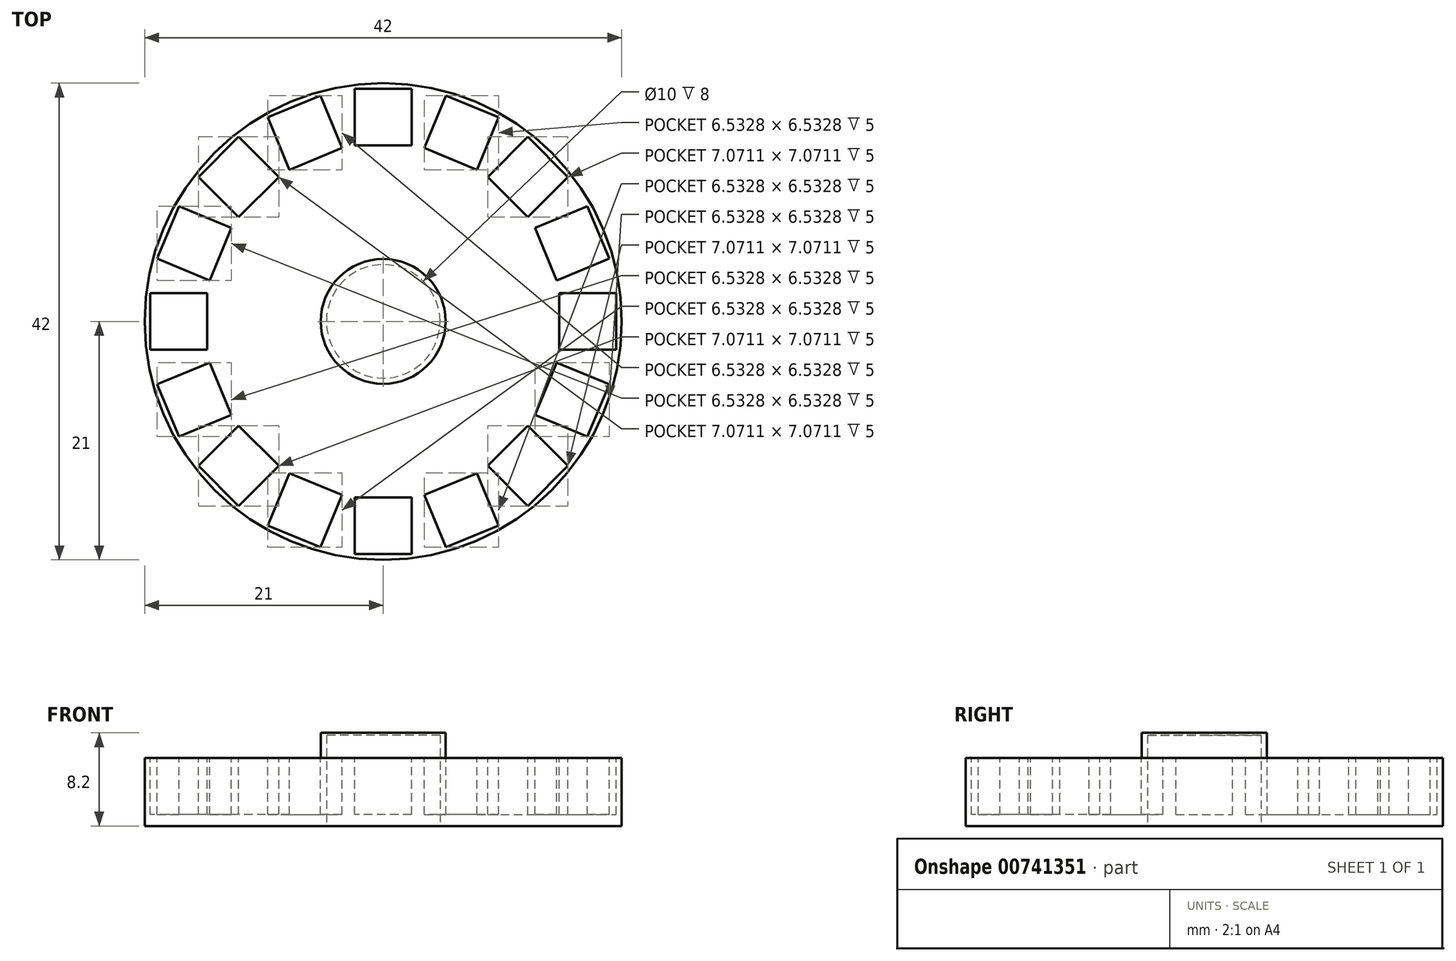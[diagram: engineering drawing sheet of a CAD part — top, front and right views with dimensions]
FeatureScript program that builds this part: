
annotation { "Feature Type Name" : "Feature", "Feature Type Description" : "" }
export const myFeature = defineFeature(function(context is Context, id is Id, definition is map)
    precondition{}
    {
        {
            var Q0;
            Q0=qCreatedBy(makeId("Front.planeOp"),FACE);
            var sketch = newSketch(context, id + "F0", { "sketchPlane" : qUnion([Q0])});
            skLineSegment(sketch, "E0", {"start": v(0, 0) * mm, "end": v(21, 0) * mm});
            skLineSegment(sketch, "E1", {"start": v(21, 0) * mm, "end": v(21, 6) * mm});
            skLineSegment(sketch, "E2", {"start": v(21, 6) * mm, "end": v(0, 6) * mm});
            skLineSegment(sketch, "E3", {"start": v(0, 6) * mm, "end": v(0, 0) * mm});
            skSolve(sketch);
        }
        {
            var Q0;
            Q0=qSketchRegion(id+"F0",true);
            var Q1;
            Q1=sQuery(id+"F0.wireOp",EDGE,"E3");
            revolve(context, id + "F1", {"surfaceOperationType" : NewSurfaceOperationType.NEW, "entities" : qUnion([Q0]), "axis" : qUnion([Q1]), "revolveType" : RevolveType.FULL});
        }
        {
            var Q0;
            Q0=qCreatedBy(makeId("Top.planeOp"),FACE);
            var sketch = newSketch(context, id + "F2", { "sketchPlane" : qUnion([Q0])});
            skCircle(sketch, "E4", {"center": v(0, 0) * mm, "radius": 11 * mm});
            skCircle(sketch, "E5", {"center": v(0, 0) * mm, "radius": 16 * mm});
            skCircle(sketch, "E6", {"center": v(0, 0) * mm, "radius": 21 * mm});
            skCircle(sketch, "E7", {"center": v(0, 0) * mm, "radius": 5 * mm});
            skCircle(sketch, "E8", {"center": v(0, 0) * mm, "radius": 5.5 * mm});
            skSolve(sketch);
        }
        {
            var Q0;
            Q0=makeQuery(id+"F2.imprint","IMPRINT",FACE,{"disambiguationData":[TD([[makeQuery(id+"F2.imprint","IMPRINT",EDGE,{"derivedFrom":sQuery(id+"F2.wireOp",EDGE,"E7")}),1.0]])]});
            extrude(context, id + "F3", {"entities" : qUnion([Q0]), "operationType" : NewBodyOperationType.REMOVE, "depth" : 25 * mm, "offsetDistance" : 25 * mm});
        }
        {
            var Q0;
            Q0=makeQuery(id+"F1.opRevolve","SWEPT_FACE",FACE,{"disambiguationData":[OSD([sQuery(id+"F0.wireOp",EDGE,"E2")])]});
            var sketch = newSketch(context, id + "F4", { "sketchPlane" : qUnion([Q0])});
            skLineSegment(sketch, "E9.bottom", {"start": v(2.5, 15.5) * mm, "end": v(-2.5, 15.5) * mm});
            skLineSegment(sketch, "E9.top", {"start": v(2.5, 20.5) * mm, "end": v(-2.5, 20.5) * mm});
            skLineSegment(sketch, "E9.left", {"start": v(2.5, 15.5) * mm, "end": v(2.5, 20.5) * mm});
            skLineSegment(sketch, "E9.right", {"start": v(-2.5, 15.5) * mm, "end": v(-2.5, 20.5) * mm});
            skLineSegment(sketch, "E10", {"start": v(0, 0) * mm, "end": v(0, 15.5) * mm, "construction": true});
            skLineSegment(sketch, "E11.1.0", {"start": v(-8.24, 13.36) * mm, "end": v(-10.15, 17.98) * mm});
            skLineSegment(sketch, "E11.1.1", {"start": v(-5.54, 19.9) * mm, "end": v(-10.15, 17.98) * mm});
            skLineSegment(sketch, "E11.1.2", {"start": v(-3.62, 15.28) * mm, "end": v(-5.54, 19.9) * mm});
            skLineSegment(sketch, "E11.1.3", {"start": v(-3.62, 15.28) * mm, "end": v(-8.24, 13.36) * mm});
            skLineSegment(sketch, "E11.2.0", {"start": v(-12.73, 9.2) * mm, "end": v(-16.26, 12.73) * mm});
            skLineSegment(sketch, "E11.2.1", {"start": v(-12.73, 16.26) * mm, "end": v(-16.26, 12.73) * mm});
            skLineSegment(sketch, "E11.2.2", {"start": v(-9.2, 12.73) * mm, "end": v(-12.73, 16.26) * mm});
            skLineSegment(sketch, "E11.2.3", {"start": v(-9.2, 12.73) * mm, "end": v(-12.73, 9.2) * mm});
            skLineSegment(sketch, "E11.3.0", {"start": v(-15.28, 3.62) * mm, "end": v(-19.9, 5.54) * mm});
            skLineSegment(sketch, "E11.3.1", {"start": v(-17.98, 10.15) * mm, "end": v(-19.9, 5.54) * mm});
            skLineSegment(sketch, "E11.3.2", {"start": v(-13.36, 8.24) * mm, "end": v(-17.98, 10.15) * mm});
            skLineSegment(sketch, "E11.3.3", {"start": v(-13.36, 8.24) * mm, "end": v(-15.28, 3.62) * mm});
            skLineSegment(sketch, "E11.4.0", {"start": v(-15.5, -2.5) * mm, "end": v(-20.5, -2.5) * mm});
            skLineSegment(sketch, "E11.4.1", {"start": v(-20.5, 2.5) * mm, "end": v(-20.5, -2.5) * mm});
            skLineSegment(sketch, "E11.4.2", {"start": v(-15.5, 2.5) * mm, "end": v(-20.5, 2.5) * mm});
            skLineSegment(sketch, "E11.4.3", {"start": v(-15.5, 2.5) * mm, "end": v(-15.5, -2.5) * mm});
            skLineSegment(sketch, "E11.5.0", {"start": v(-13.36, -8.24) * mm, "end": v(-17.98, -10.15) * mm});
            skLineSegment(sketch, "E11.5.1", {"start": v(-19.9, -5.54) * mm, "end": v(-17.98, -10.15) * mm});
            skLineSegment(sketch, "E11.5.2", {"start": v(-15.28, -3.62) * mm, "end": v(-19.9, -5.54) * mm});
            skLineSegment(sketch, "E11.5.3", {"start": v(-15.28, -3.62) * mm, "end": v(-13.36, -8.24) * mm});
            skLineSegment(sketch, "E11.6.0", {"start": v(-9.2, -12.73) * mm, "end": v(-12.73, -16.26) * mm});
            skLineSegment(sketch, "E11.6.1", {"start": v(-16.26, -12.73) * mm, "end": v(-12.73, -16.26) * mm});
            skLineSegment(sketch, "E11.6.2", {"start": v(-12.73, -9.2) * mm, "end": v(-16.26, -12.73) * mm});
            skLineSegment(sketch, "E11.6.3", {"start": v(-12.73, -9.2) * mm, "end": v(-9.2, -12.73) * mm});
            skLineSegment(sketch, "E11.7.0", {"start": v(-3.62, -15.28) * mm, "end": v(-5.54, -19.9) * mm});
            skLineSegment(sketch, "E11.7.1", {"start": v(-10.15, -17.98) * mm, "end": v(-5.54, -19.9) * mm});
            skLineSegment(sketch, "E11.7.2", {"start": v(-8.24, -13.36) * mm, "end": v(-10.15, -17.98) * mm});
            skLineSegment(sketch, "E11.7.3", {"start": v(-8.24, -13.36) * mm, "end": v(-3.62, -15.28) * mm});
            skLineSegment(sketch, "E11.8.0", {"start": v(2.5, -15.5) * mm, "end": v(2.5, -20.5) * mm});
            skLineSegment(sketch, "E11.8.1", {"start": v(-2.5, -20.5) * mm, "end": v(2.5, -20.5) * mm});
            skLineSegment(sketch, "E11.8.2", {"start": v(-2.5, -15.5) * mm, "end": v(-2.5, -20.5) * mm});
            skLineSegment(sketch, "E11.8.3", {"start": v(-2.5, -15.5) * mm, "end": v(2.5, -15.5) * mm});
            skLineSegment(sketch, "E11.9.0", {"start": v(8.24, -13.36) * mm, "end": v(10.15, -17.98) * mm});
            skLineSegment(sketch, "E11.9.1", {"start": v(5.54, -19.9) * mm, "end": v(10.15, -17.98) * mm});
            skLineSegment(sketch, "E11.9.2", {"start": v(3.62, -15.28) * mm, "end": v(5.54, -19.9) * mm});
            skLineSegment(sketch, "E11.9.3", {"start": v(3.62, -15.28) * mm, "end": v(8.24, -13.36) * mm});
            skLineSegment(sketch, "E11.10.0", {"start": v(12.73, -9.2) * mm, "end": v(16.26, -12.73) * mm});
            skLineSegment(sketch, "E11.10.1", {"start": v(12.73, -16.26) * mm, "end": v(16.26, -12.73) * mm});
            skLineSegment(sketch, "E11.10.2", {"start": v(9.2, -12.73) * mm, "end": v(12.73, -16.26) * mm});
            skLineSegment(sketch, "E11.10.3", {"start": v(9.2, -12.73) * mm, "end": v(12.73, -9.2) * mm});
            skLineSegment(sketch, "E11.11.0", {"start": v(15.28, -3.62) * mm, "end": v(19.9, -5.54) * mm});
            skLineSegment(sketch, "E11.11.1", {"start": v(17.98, -10.15) * mm, "end": v(19.9, -5.54) * mm});
            skLineSegment(sketch, "E11.11.2", {"start": v(13.36, -8.24) * mm, "end": v(17.98, -10.15) * mm});
            skLineSegment(sketch, "E11.11.3", {"start": v(13.36, -8.24) * mm, "end": v(15.28, -3.62) * mm});
            skLineSegment(sketch, "E11.12.0", {"start": v(15.5, 2.5) * mm, "end": v(20.5, 2.5) * mm});
            skLineSegment(sketch, "E11.12.1", {"start": v(20.5, -2.5) * mm, "end": v(20.5, 2.5) * mm});
            skLineSegment(sketch, "E11.12.2", {"start": v(15.5, -2.5) * mm, "end": v(20.5, -2.5) * mm});
            skLineSegment(sketch, "E11.12.3", {"start": v(15.5, -2.5) * mm, "end": v(15.5, 2.5) * mm});
            skLineSegment(sketch, "E11.13.0", {"start": v(13.36, 8.24) * mm, "end": v(17.98, 10.15) * mm});
            skLineSegment(sketch, "E11.13.1", {"start": v(19.9, 5.54) * mm, "end": v(17.98, 10.15) * mm});
            skLineSegment(sketch, "E11.13.2", {"start": v(15.28, 3.62) * mm, "end": v(19.9, 5.54) * mm});
            skLineSegment(sketch, "E11.13.3", {"start": v(15.28, 3.62) * mm, "end": v(13.36, 8.24) * mm});
            skLineSegment(sketch, "E11.14.0", {"start": v(9.2, 12.73) * mm, "end": v(12.73, 16.26) * mm});
            skLineSegment(sketch, "E11.14.1", {"start": v(16.26, 12.73) * mm, "end": v(12.73, 16.26) * mm});
            skLineSegment(sketch, "E11.14.2", {"start": v(12.73, 9.2) * mm, "end": v(16.26, 12.73) * mm});
            skLineSegment(sketch, "E11.14.3", {"start": v(12.73, 9.2) * mm, "end": v(9.2, 12.73) * mm});
            skLineSegment(sketch, "E11.15.0", {"start": v(3.62, 15.28) * mm, "end": v(5.54, 19.9) * mm});
            skLineSegment(sketch, "E11.15.1", {"start": v(10.15, 17.98) * mm, "end": v(5.54, 19.9) * mm});
            skLineSegment(sketch, "E11.15.2", {"start": v(8.24, 13.36) * mm, "end": v(10.15, 17.98) * mm});
            skLineSegment(sketch, "E11.15.3", {"start": v(8.24, 13.36) * mm, "end": v(3.62, 15.28) * mm});
            skPoint(sketch, "E11.center", {"position": v(0, 0) * mm});
            skSolve(sketch);
        }
        {
            var Q0;
            {var subQ0=sQuery(id+"F4.wireOp",EDGE,"6b0e4d02-cffa-4799-8ca5-8f1609af44a9.1.3");Q0=makeQuery(id+"F4.imprint","IMPRINT",FACE,{"disambiguationData":[TD([[makeQuery(id+"F4.imprint","IMPRINT",EDGE,{"derivedFrom":subQ0}),-1.0]])]});}
            var Q1;
            {var subQ0=sQuery(id+"F4.wireOp",EDGE,"E9.bottom");Q1=makeQuery(id+"F4.imprint","IMPRINT",FACE,{"disambiguationData":[TD([[makeQuery(id+"F4.imprint","IMPRINT",EDGE,{"derivedFrom":subQ0}),-1.0]])]});}
            var Q2;
            {var subQ0=sQuery(id+"F4.wireOp",EDGE,"90cd43ab-74c5-4661-9c80-5ee8405ae9ff.9.15.0");Q2=makeQuery(id+"F4.imprint","IMPRINT",FACE,{"disambiguationData":[TD([[makeQuery(id+"F4.imprint","IMPRINT",EDGE,{"derivedFrom":subQ0}),-1.0]])]});}
            var Q3;
            {var subQ0=sQuery(id+"F4.wireOp",EDGE,"90cd43ab-74c5-4661-9c80-5ee8405ae9ff.9.14.0");Q3=makeQuery(id+"F4.imprint","IMPRINT",FACE,{"disambiguationData":[TD([[makeQuery(id+"F4.imprint","IMPRINT",EDGE,{"derivedFrom":subQ0}),-1.0]])]});}
            var Q4;
            {var subQ0=sQuery(id+"F4.wireOp",EDGE,"90cd43ab-74c5-4661-9c80-5ee8405ae9ff.9.13.0");Q4=makeQuery(id+"F4.imprint","IMPRINT",FACE,{"disambiguationData":[TD([[makeQuery(id+"F4.imprint","IMPRINT",EDGE,{"derivedFrom":subQ0}),-1.0]])]});}
            var Q5;
            {var subQ0=sQuery(id+"F4.wireOp",EDGE,"90cd43ab-74c5-4661-9c80-5ee8405ae9ff.9.12.0");Q5=makeQuery(id+"F4.imprint","IMPRINT",FACE,{"disambiguationData":[TD([[makeQuery(id+"F4.imprint","IMPRINT",EDGE,{"derivedFrom":subQ0}),-1.0]])]});}
            var Q6;
            {var subQ0=sQuery(id+"F4.wireOp",EDGE,"90cd43ab-74c5-4661-9c80-5ee8405ae9ff.9.11.0");Q6=makeQuery(id+"F4.imprint","IMPRINT",FACE,{"disambiguationData":[TD([[makeQuery(id+"F4.imprint","IMPRINT",EDGE,{"derivedFrom":subQ0}),-1.0]])]});}
            var Q7;
            {var subQ0=sQuery(id+"F4.wireOp",EDGE,"90cd43ab-74c5-4661-9c80-5ee8405ae9ff.9.10.0");Q7=makeQuery(id+"F4.imprint","IMPRINT",FACE,{"disambiguationData":[TD([[makeQuery(id+"F4.imprint","IMPRINT",EDGE,{"derivedFrom":subQ0}),-1.0]])]});}
            var Q8;
            {var subQ0=sQuery(id+"F4.wireOp",EDGE,"90cd43ab-74c5-4661-9c80-5ee8405ae9ff.9.9.0");Q8=makeQuery(id+"F4.imprint","IMPRINT",FACE,{"disambiguationData":[TD([[makeQuery(id+"F4.imprint","IMPRINT",EDGE,{"derivedFrom":subQ0}),-1.0]])]});}
            var Q9;
            {var subQ0=sQuery(id+"F4.wireOp",EDGE,"90cd43ab-74c5-4661-9c80-5ee8405ae9ff.9.8.0");Q9=makeQuery(id+"F4.imprint","IMPRINT",FACE,{"disambiguationData":[TD([[makeQuery(id+"F4.imprint","IMPRINT",EDGE,{"derivedFrom":subQ0}),-1.0]])]});}
            var Q10;
            {var subQ0=sQuery(id+"F4.wireOp",EDGE,"90cd43ab-74c5-4661-9c80-5ee8405ae9ff.9.7.0");Q10=makeQuery(id+"F4.imprint","IMPRINT",FACE,{"disambiguationData":[TD([[makeQuery(id+"F4.imprint","IMPRINT",EDGE,{"derivedFrom":subQ0}),-1.0]])]});}
            var Q11;
            {var subQ0=sQuery(id+"F4.wireOp",EDGE,"90cd43ab-74c5-4661-9c80-5ee8405ae9ff.9.6.0");Q11=makeQuery(id+"F4.imprint","IMPRINT",FACE,{"disambiguationData":[TD([[makeQuery(id+"F4.imprint","IMPRINT",EDGE,{"derivedFrom":subQ0}),-1.0]])]});}
            var Q12;
            {var subQ0=sQuery(id+"F4.wireOp",EDGE,"90cd43ab-74c5-4661-9c80-5ee8405ae9ff.9.5.0");Q12=makeQuery(id+"F4.imprint","IMPRINT",FACE,{"disambiguationData":[TD([[makeQuery(id+"F4.imprint","IMPRINT",EDGE,{"derivedFrom":subQ0}),-1.0]])]});}
            var Q13;
            {var subQ0=sQuery(id+"F4.wireOp",EDGE,"90cd43ab-74c5-4661-9c80-5ee8405ae9ff.9.4.0");Q13=makeQuery(id+"F4.imprint","IMPRINT",FACE,{"disambiguationData":[TD([[makeQuery(id+"F4.imprint","IMPRINT",EDGE,{"derivedFrom":subQ0}),-1.0]])]});}
            var Q14;
            {var subQ0=sQuery(id+"F4.wireOp",EDGE,"90cd43ab-74c5-4661-9c80-5ee8405ae9ff.9.3.0");Q14=makeQuery(id+"F4.imprint","IMPRINT",FACE,{"disambiguationData":[TD([[makeQuery(id+"F4.imprint","IMPRINT",EDGE,{"derivedFrom":subQ0}),-1.0]])]});}
            var Q15;
            {var subQ0=sQuery(id+"F4.wireOp",EDGE,"6b0e4d02-cffa-4799-8ca5-8f1609af44a9.2.3");Q15=makeQuery(id+"F4.imprint","IMPRINT",FACE,{"disambiguationData":[TD([[makeQuery(id+"F4.imprint","IMPRINT",EDGE,{"derivedFrom":subQ0}),-1.0]])]});}
            var Q16;
            Q16=makeQuery(id+"F4.imprint","IMPRINT",FACE,{"disambiguationData":[TD([[makeQuery(id+"F4.imprint","IMPRINT",EDGE,{"derivedFrom":sQuery(id+"F4.wireOp",EDGE,"E11.15.0")}),-1.0]])]});
            var Q17;
            Q17=makeQuery(id+"F4.imprint","IMPRINT",FACE,{"disambiguationData":[TD([[makeQuery(id+"F4.imprint","IMPRINT",EDGE,{"derivedFrom":sQuery(id+"F4.wireOp",EDGE,"E11.14.0")}),-1.0]])]});
            var Q18;
            Q18=makeQuery(id+"F4.imprint","IMPRINT",FACE,{"disambiguationData":[TD([[makeQuery(id+"F4.imprint","IMPRINT",EDGE,{"derivedFrom":sQuery(id+"F4.wireOp",EDGE,"E11.13.0")}),-1.0]])]});
            var Q19;
            Q19=makeQuery(id+"F4.imprint","IMPRINT",FACE,{"disambiguationData":[TD([[makeQuery(id+"F4.imprint","IMPRINT",EDGE,{"derivedFrom":sQuery(id+"F4.wireOp",EDGE,"E11.12.0")}),-1.0]])]});
            var Q20;
            Q20=makeQuery(id+"F4.imprint","IMPRINT",FACE,{"disambiguationData":[TD([[makeQuery(id+"F4.imprint","IMPRINT",EDGE,{"derivedFrom":sQuery(id+"F4.wireOp",EDGE,"E11.11.0")}),-1.0]])]});
            var Q21;
            Q21=makeQuery(id+"F4.imprint","IMPRINT",FACE,{"disambiguationData":[TD([[makeQuery(id+"F4.imprint","IMPRINT",EDGE,{"derivedFrom":sQuery(id+"F4.wireOp",EDGE,"E11.10.0")}),-1.0]])]});
            var Q22;
            Q22=makeQuery(id+"F4.imprint","IMPRINT",FACE,{"disambiguationData":[TD([[makeQuery(id+"F4.imprint","IMPRINT",EDGE,{"derivedFrom":sQuery(id+"F4.wireOp",EDGE,"E11.9.0")}),-1.0]])]});
            var Q23;
            Q23=makeQuery(id+"F4.imprint","IMPRINT",FACE,{"disambiguationData":[TD([[makeQuery(id+"F4.imprint","IMPRINT",EDGE,{"derivedFrom":sQuery(id+"F4.wireOp",EDGE,"E11.8.0")}),-1.0]])]});
            var Q24;
            Q24=makeQuery(id+"F4.imprint","IMPRINT",FACE,{"disambiguationData":[TD([[makeQuery(id+"F4.imprint","IMPRINT",EDGE,{"derivedFrom":sQuery(id+"F4.wireOp",EDGE,"E11.7.0")}),-1.0]])]});
            var Q25;
            Q25=makeQuery(id+"F4.imprint","IMPRINT",FACE,{"disambiguationData":[TD([[makeQuery(id+"F4.imprint","IMPRINT",EDGE,{"derivedFrom":sQuery(id+"F4.wireOp",EDGE,"E11.6.0")}),-1.0]])]});
            var Q26;
            Q26=makeQuery(id+"F4.imprint","IMPRINT",FACE,{"disambiguationData":[TD([[makeQuery(id+"F4.imprint","IMPRINT",EDGE,{"derivedFrom":sQuery(id+"F4.wireOp",EDGE,"E11.5.0")}),-1.0]])]});
            var Q27;
            Q27=makeQuery(id+"F4.imprint","IMPRINT",FACE,{"disambiguationData":[TD([[makeQuery(id+"F4.imprint","IMPRINT",EDGE,{"derivedFrom":sQuery(id+"F4.wireOp",EDGE,"E11.4.0")}),-1.0]])]});
            var Q28;
            Q28=makeQuery(id+"F4.imprint","IMPRINT",FACE,{"disambiguationData":[TD([[makeQuery(id+"F4.imprint","IMPRINT",EDGE,{"derivedFrom":sQuery(id+"F4.wireOp",EDGE,"E11.3.0")}),-1.0]])]});
            var Q29;
            Q29=makeQuery(id+"F4.imprint","IMPRINT",FACE,{"disambiguationData":[TD([[makeQuery(id+"F4.imprint","IMPRINT",EDGE,{"derivedFrom":sQuery(id+"F4.wireOp",EDGE,"E11.2.0")}),-1.0]])]});
            var Q30;
            Q30=makeQuery(id+"F4.imprint","IMPRINT",FACE,{"disambiguationData":[TD([[makeQuery(id+"F4.imprint","IMPRINT",EDGE,{"derivedFrom":sQuery(id+"F4.wireOp",EDGE,"E11.1.0")}),-1.0]])]});
            extrude(context, id + "F5", {"entities" : qUnion([Q0, Q1, Q2, Q3, Q4, Q5, Q6, Q7, Q8, Q9, Q10, Q11, Q12, Q13, Q14, Q15, Q16, Q17, Q18, Q19, Q20, Q21, Q22, Q23, Q24, Q25, Q26, Q27, Q28, Q29, Q30]), "operationType" : NewBodyOperationType.REMOVE, "oppositeDirection" : true, "depth" : 5 * mm, "offsetDistance" : 25 * mm});
        }
        {
            var Q0;
            Q0=makeQuery(id+"F2.imprint","IMPRINT",FACE,{"disambiguationData":[TD([[makeQuery(id+"F2.imprint","IMPRINT",EDGE,{"derivedFrom":sQuery(id+"F2.wireOp",EDGE,"E7")}),-1.0]])]});
            extrude(context, id + "F6", {"entities" : qUnion([Q0]), "operationType" : NewBodyOperationType.ADD, "depth" : 8.2 * mm, "offsetDistance" : 25 * mm});
        }
        {
            var Q0;
            Q0=qCreatedBy(makeId("Right.planeOp"),FACE);
            var sketch = newSketch(context, id + "F7", { "sketchPlane" : qUnion([Q0])});
            skLineSegment(sketch, "E12", {"start": v(0, 0) * mm, "end": v(0, 8.2) * mm});
            skLineSegment(sketch, "E13.bottom", {"start": v(0, 8.2) * mm, "end": v(5.48, 8.2) * mm});
            skLineSegment(sketch, "E13.top", {"start": v(0, 8.2) * mm, "end": v(5.48, 8.2) * mm});
            skLineSegment(sketch, "E13.left", {"start": v(0, 8.2) * mm, "end": v(0, 8.2) * mm});
            skLineSegment(sketch, "E13.right", {"start": v(5.48, 8.2) * mm, "end": v(5.48, 8.2) * mm});
            skLineSegment(sketch, "E14.bottom", {"start": v(0, 8.2) * mm, "end": v(5.5, 8.2) * mm});
            skLineSegment(sketch, "E14.top", {"start": v(0, 8) * mm, "end": v(5.5, 8) * mm});
            skLineSegment(sketch, "E14.left", {"start": v(0, 8.2) * mm, "end": v(0, 8) * mm});
            skLineSegment(sketch, "E14.right", {"start": v(5.5, 8.2) * mm, "end": v(5.5, 8) * mm});
            skSolve(sketch);
        }
        {
            var Q0;
            Q0=makeQuery(id+"F7.imprint","IMPRINT",FACE,{"disambiguationData":[TD([[makeQuery(id+"F7.imprint","IMPRINT",EDGE,{"derivedFrom":sQuery(id+"F7.wireOp",EDGE,"E14.top")}),1.0]])]});
            var Q1;
            Q1=sQuery(id+"F7.wireOp",EDGE,"E14.left");
            revolve(context, id + "F8", {"operationType" : NewBodyOperationType.ADD, "surfaceOperationType" : NewSurfaceOperationType.NEW, "entities" : qUnion([Q0]), "axis" : qUnion([Q1]), "revolveType" : RevolveType.FULL});
        }
    });
